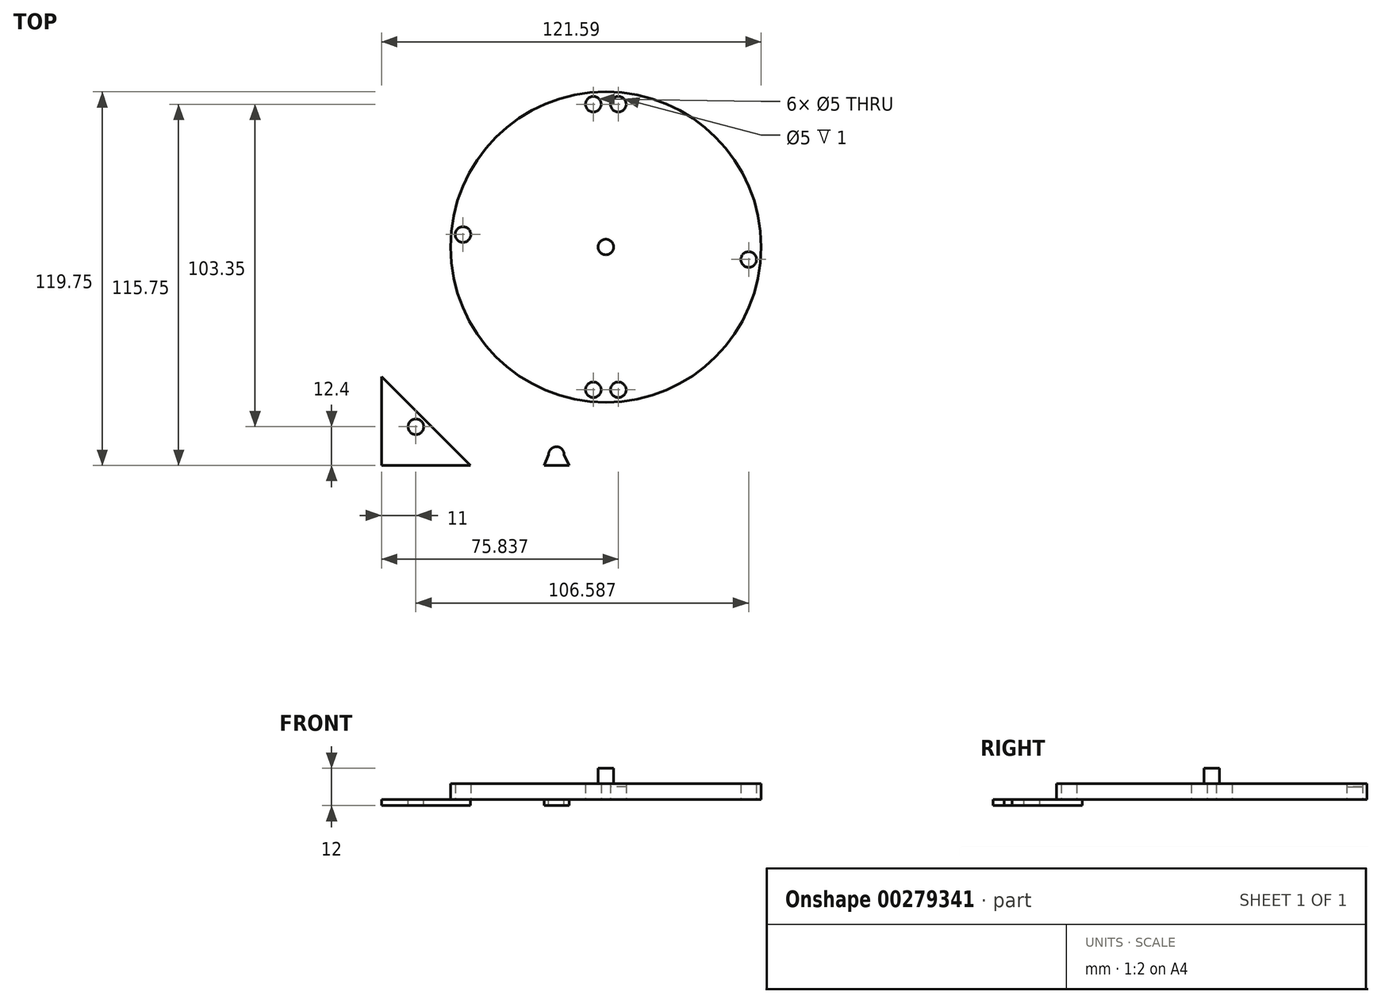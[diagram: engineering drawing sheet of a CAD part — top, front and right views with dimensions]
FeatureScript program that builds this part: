
annotation { "Feature Type Name" : "Feature", "Feature Type Description" : "" }
export const myFeature = defineFeature(function(context is Context, id is Id, definition is map)
    precondition{}
    {
        {
            var Q0;
            Q0=qCreatedBy(makeId("Top.planeOp"),FACE);
            var sketch = newSketch(context, id + "F0", { "sketchPlane" : qUnion([Q0])});
            skLineSegment(sketch, "E0.bottom", {"start": v(75, 70) * mm, "end": v(-75, 70) * mm});
            skLineSegment(sketch, "E0.top", {"start": v(75, -70) * mm, "end": v(-75, -70) * mm});
            skLineSegment(sketch, "E0.left", {"start": v(75, 70) * mm, "end": v(75, -70) * mm});
            skLineSegment(sketch, "E0.right", {"start": v(-75, 70) * mm, "end": v(-75, -70) * mm});
            skPoint(sketch, "E0.middle", {"position": v(0, 0) * mm});
            skSolve(sketch);
        }
        {
            var Q0;
            Q0=qSketchRegion(id+"F0",true);
            extrude(context, id + "F1", {"entities" : qUnion([Q0]), "depth" : 2 * mm});
        }
        {
            var Q0;
            Q0=makeQuery(id+"F1.opExtrude","CAP_FACE",FACE,{"disambiguationData":[OSD([sQuery(id+"F0.wireOp",EDGE,"E0.bottom"),sQuery(id+"F0.wireOp",EDGE,"E0.top"),sQuery(id+"F0.wireOp",EDGE,"E0.left"),sQuery(id+"F0.wireOp",EDGE,"E0.right")])],"isStart":false});
            var sketch = newSketch(context, id + "F2", { "sketchPlane" : qUnion([Q0])});
            skArc(sketch, "E1", {"start": v(-67.18, 6.35) * mm, "mid": v(-67.92, 8.12) * mm, "end": v(-69.68, 8.85) * mm});
            skArc(sketch, "E2.MirrorC", {"start": v(-67.18, -6.35) * mm, "mid": v(-67.92, -8.12) * mm, "end": v(-69.68, -8.85) * mm});
            skArc(sketch, "E3", {"start": v(-21.5, 66.52) * mm, "mid": v(-19, 64) * mm, "end": v(-16.5, 66.52) * mm});
            skCircle(sketch, "E4", {"center": v(-64, 57.6) * mm, "radius": 2.5 * mm});
            skArc(sketch, "E5.MirrorC", {"start": v(-21.5, -66.52) * mm, "mid": v(-19, -64) * mm, "end": v(-16.5, -66.52) * mm});
            skCircle(sketch, "E6.MirrorC", {"center": v(-64, -57.6) * mm, "radius": 2.5 * mm});
            skLineSegment(sketch, "E7", {"start": v(-21.5, 66.52) * mm, "end": v(-22.94, 70) * mm});
            skLineSegment(sketch, "E8.MirrorCS", {"start": v(-16.5, 66.52) * mm, "end": v(-14.88, 70) * mm});
            skLineSegment(sketch, "E9.MirrorCS", {"start": v(-16.5, -66.52) * mm, "end": v(-14.88, -70) * mm});
            skLineSegment(sketch, "E10.MirrorCS", {"start": v(-21.5, -66.52) * mm, "end": v(-22.94, -70) * mm});
            skLineSegment(sketch, "E11", {"start": v(-46.5, 70) * mm, "end": v(-75, 41.5) * mm});
            skLineSegment(sketch, "E12.MirrorCS", {"start": v(-46.5, -70) * mm, "end": v(-75, -41.5) * mm});
            skLineSegment(sketch, "E13", {"start": v(-69.68, 8.85) * mm, "end": v(-75, 8.85) * mm});
            skLineSegment(sketch, "E14", {"start": v(-67.18, -6.35) * mm, "end": v(-67.18, 6.35) * mm});
            skLineSegment(sketch, "E15.MirrorCS", {"start": v(-69.68, -8.85) * mm, "end": v(-75, -8.85) * mm});
            skSolve(sketch);
        }
        {
            var Q0;
            Q0=qSketchRegion(id+"F2",true);
            var Q1;
            Q1=makeQuery(id+"F2.imprint","IMPRINT",FACE,{"disambiguationData":[TD([[makeQuery(id+"F2.imprint","IMPRINT",EDGE,{"derivedFrom":sQuery(id+"F2.wireOp",EDGE,"E4")}),-1.0]])]});
            var Q2;
            Q2=makeQuery(id+"F2.imprint","IMPRINT",FACE,{"disambiguationData":[TD([[makeQuery(id+"F2.imprint","IMPRINT",EDGE,{"derivedFrom":sQuery(id+"F2.wireOp",EDGE,"E1")}),1.0]])]});
            var Q3;
            Q3=makeQuery(id+"F2.imprint","IMPRINT",FACE,{"disambiguationData":[TD([[makeQuery(id+"F2.imprint","IMPRINT",EDGE,{"derivedFrom":sQuery(id+"F2.wireOp",EDGE,"E5.MirrorC")}),-1.0]])]});
            var Q4;
            Q4=makeQuery(id+"F2.imprint","IMPRINT",FACE,{"disambiguationData":[TD([[makeQuery(id+"F2.imprint","IMPRINT",EDGE,{"derivedFrom":sQuery(id+"F2.wireOp",EDGE,"E3")}),1.0]])]});
            var Q5;
            Q5=makeQuery(id+"F2.imprint","IMPRINT",FACE,{"disambiguationData":[TD([[makeQuery(id+"F2.imprint","IMPRINT",EDGE,{"derivedFrom":sQuery(id+"F2.wireOp",EDGE,"E6.MirrorC")}),1.0]])]});
            extrude(context, id + "F3", {"entities" : qUnion([Q0, Q1, Q2, Q3, Q4, Q5]), "operationType" : NewBodyOperationType.REMOVE, "oppositeDirection" : true, "depth" : 5 * mm});
        }
        {
            var Q0;
            Q0=makeQuery(id+"F1.opExtrude","CAP_FACE",FACE,{"disambiguationData":[OSD([sQuery(id+"F0.wireOp",EDGE,"E0.bottom"),sQuery(id+"F0.wireOp",EDGE,"E0.top"),sQuery(id+"F0.wireOp",EDGE,"E0.left"),sQuery(id+"F0.wireOp",EDGE,"E0.right")])],"isStart":false});
            var sketch = newSketch(context, id + "F4", { "sketchPlane" : qUnion([Q0])});
            skCircle(sketch, "E16", {"center": v(-3.16, 0) * mm, "radius": 49.75 * mm});
            skLineSegment(sketch, "E17", {"start": v(-3.16, 0) * mm, "end": v(-53.16, 0) * mm});
            skLineSegment(sketch, "E18", {"start": v(-3.16, 0) * mm, "end": v(-3.16, 49.75) * mm});
            skLineSegment(sketch, "E19", {"start": v(-3.16, 0) * mm, "end": v(46.59, 0) * mm});
            skLineSegment(sketch, "E20", {"start": v(-3.16, 0) * mm, "end": v(-3.16, -49.75) * mm});
            skCircle(sketch, "E21", {"center": v(-7.16, 45.75) * mm, "radius": 2.5 * mm});
            skCircle(sketch, "E22.MirrorC", {"center": v(0.84, 45.75) * mm, "radius": 2.5 * mm});
            skCircle(sketch, "E23.1.0", {"center": v(-48.91, 4) * mm, "radius": 2.5 * mm});
            skCircle(sketch, "E23.1.1", {"center": v(-48.91, -4) * mm, "radius": 2.5 * mm});
            skCircle(sketch, "E23.2.0", {"center": v(-7.16, -45.75) * mm, "radius": 2.5 * mm});
            skCircle(sketch, "E23.2.1", {"center": v(0.84, -45.75) * mm, "radius": 2.5 * mm});
            skCircle(sketch, "E23.3.0", {"center": v(42.59, -4) * mm, "radius": 2.5 * mm});
            skCircle(sketch, "E23.3.1", {"center": v(42.59, 4) * mm, "radius": 2.5 * mm});
            skCircle(sketch, "E24", {"center": v(-3.16, 0) * mm, "radius": 2.5 * mm});
            skSolve(sketch);
        }
        {
            var Q0;
            Q0=makeQuery(id+"F4.imprint","IMPRINT",FACE,{"disambiguationData":[TD([[makeQuery(id+"F4.imprint","IMPRINT",EDGE,{"derivedFrom":sQuery(id+"F4.wireOp",EDGE,"E21")}),-1.0]])]});
            var Q1;
            Q1=makeQuery(id+"F4.imprint","IMPRINT",FACE,{"disambiguationData":[TD([[makeQuery(id+"F4.imprint","IMPRINT",EDGE,{"derivedFrom":sQuery(id+"F4.wireOp",EDGE,"E23.2.1")}),-1.0]])]});
            var Q2;
            Q2=makeQuery(id+"F4.imprint","IMPRINT",FACE,{"disambiguationData":[TD([[makeQuery(id+"F4.imprint","IMPRINT",EDGE,{"derivedFrom":sQuery(id+"F4.wireOp",EDGE,"E22.MirrorC")}),-1.0]])]});
            var Q3;
            Q3=makeQuery(id+"F4.imprint","IMPRINT",FACE,{"disambiguationData":[TD([[makeQuery(id+"F4.imprint","IMPRINT",EDGE,{"derivedFrom":sQuery(id+"F4.wireOp",EDGE,"E23.3.1")}),1.0]])]});
            var Q4;
            Q4=makeQuery(id+"F4.imprint","IMPRINT",FACE,{"disambiguationData":[TD([[makeQuery(id+"F4.imprint","IMPRINT",EDGE,{"derivedFrom":sQuery(id+"F4.wireOp",EDGE,"E23.2.0")}),-1.0]])]});
            var Q5;
            Q5=makeQuery(id+"F4.imprint","IMPRINT",FACE,{"disambiguationData":[TD([[makeQuery(id+"F4.imprint","IMPRINT",EDGE,{"derivedFrom":sQuery(id+"F4.wireOp",EDGE,"E23.1.1")}),1.0]])]});
            var Q6;
            {var subQ1=sQuery(id+"F4.wireOp",EDGE,"E17");var subQ3=sQuery(id+"F4.wireOp",EDGE,"E24");var subQ4=makeQuery(id+"F4.imprint","INTERSECT",VERTEX,{"derivedFrom":[subQ1,subQ3]});Q6=makeQuery(id+"F4.imprint","IMPRINT",FACE,{"disambiguationData":[TD([[makeQuery(id+"F4.imprint","IMPRINT",EDGE,{"disambiguationData":[TD([[subQ4,-1.0]])],"derivedFrom":subQ3}),1.0]])]});}
            var Q7;
            {var subQ1=sQuery(id+"F4.wireOp",EDGE,"E18");var subQ3=sQuery(id+"F4.wireOp",EDGE,"E24");var subQ4=makeQuery(id+"F4.imprint","INTERSECT",VERTEX,{"derivedFrom":[subQ1,subQ3]});Q7=makeQuery(id+"F4.imprint","IMPRINT",FACE,{"disambiguationData":[TD([[makeQuery(id+"F4.imprint","IMPRINT",EDGE,{"disambiguationData":[TD([[subQ4,1.0]])],"derivedFrom":subQ3}),1.0]])]});}
            var Q8;
            {var subQ1=sQuery(id+"F4.wireOp",EDGE,"E19");var subQ3=sQuery(id+"F4.wireOp",EDGE,"E24");var subQ4=makeQuery(id+"F4.imprint","INTERSECT",VERTEX,{"derivedFrom":[subQ1,subQ3]});Q8=makeQuery(id+"F4.imprint","IMPRINT",FACE,{"disambiguationData":[TD([[makeQuery(id+"F4.imprint","IMPRINT",EDGE,{"disambiguationData":[TD([[subQ4,1.0]])],"derivedFrom":subQ3}),1.0]])]});}
            var Q9;
            {var subQ1=sQuery(id+"F4.wireOp",EDGE,"E17");var subQ3=sQuery(id+"F4.wireOp",EDGE,"E24");var subQ4=makeQuery(id+"F4.imprint","INTERSECT",VERTEX,{"derivedFrom":[subQ1,subQ3]});Q9=makeQuery(id+"F4.imprint","IMPRINT",FACE,{"disambiguationData":[TD([[makeQuery(id+"F4.imprint","IMPRINT",EDGE,{"disambiguationData":[TD([[subQ4,1.0]])],"derivedFrom":subQ3}),1.0]])]});}
            extrude(context, id + "F5", {"entities" : qUnion([Q0, Q1, Q2, Q3, Q4, Q5, Q6, Q7, Q8, Q9]), "operationType" : NewBodyOperationType.ADD, "depth" : 5 * mm});
        }
        {
            var Q0;
            Q0=makeQuery(id+"F4.imprint","IMPRINT",FACE,{"disambiguationData":[TD([[makeQuery(id+"F4.imprint","IMPRINT",EDGE,{"derivedFrom":sQuery(id+"F4.wireOp",EDGE,"E23.1.1")}),-1.0]])]});
            var Q1;
            Q1=makeQuery(id+"F4.imprint","IMPRINT",FACE,{"disambiguationData":[TD([[makeQuery(id+"F4.imprint","IMPRINT",EDGE,{"derivedFrom":sQuery(id+"F4.wireOp",EDGE,"E22.MirrorC")}),1.0]])]});
            extrude(context, id + "F6", {"entities" : qUnion([Q0, Q1]), "operationType" : NewBodyOperationType.ADD, "depth" : 4 * mm});
        }
        {
            var Q0;
            {var subQ1=sQuery(id+"F4.wireOp",EDGE,"E19");var subQ3=sQuery(id+"F4.wireOp",EDGE,"E24");var subQ4=makeQuery(id+"F4.imprint","INTERSECT",VERTEX,{"derivedFrom":[subQ1,subQ3]});Q0=makeQuery(id+"F4.imprint","IMPRINT",FACE,{"disambiguationData":[TD([[makeQuery(id+"F4.imprint","IMPRINT",EDGE,{"disambiguationData":[TD([[subQ4,1.0]])],"derivedFrom":subQ3}),1.0]])]});}
            var Q1;
            {var subQ1=sQuery(id+"F4.wireOp",EDGE,"E18");var subQ3=sQuery(id+"F4.wireOp",EDGE,"E24");var subQ4=makeQuery(id+"F4.imprint","INTERSECT",VERTEX,{"derivedFrom":[subQ1,subQ3]});Q1=makeQuery(id+"F4.imprint","IMPRINT",FACE,{"disambiguationData":[TD([[makeQuery(id+"F4.imprint","IMPRINT",EDGE,{"disambiguationData":[TD([[subQ4,1.0]])],"derivedFrom":subQ3}),1.0]])]});}
            var Q2;
            {var subQ1=sQuery(id+"F4.wireOp",EDGE,"E17");var subQ3=sQuery(id+"F4.wireOp",EDGE,"E24");var subQ4=makeQuery(id+"F4.imprint","INTERSECT",VERTEX,{"derivedFrom":[subQ1,subQ3]});Q2=makeQuery(id+"F4.imprint","IMPRINT",FACE,{"disambiguationData":[TD([[makeQuery(id+"F4.imprint","IMPRINT",EDGE,{"disambiguationData":[TD([[subQ4,1.0]])],"derivedFrom":subQ3}),1.0]])]});}
            var Q3;
            {var subQ1=sQuery(id+"F4.wireOp",EDGE,"E17");var subQ3=sQuery(id+"F4.wireOp",EDGE,"E24");var subQ4=makeQuery(id+"F4.imprint","INTERSECT",VERTEX,{"derivedFrom":[subQ1,subQ3]});Q3=makeQuery(id+"F4.imprint","IMPRINT",FACE,{"disambiguationData":[TD([[makeQuery(id+"F4.imprint","IMPRINT",EDGE,{"disambiguationData":[TD([[subQ4,-1.0]])],"derivedFrom":subQ3}),1.0]])]});}
            extrude(context, id + "F7", {"entities" : qUnion([Q0, Q1, Q2, Q3]), "operationType" : NewBodyOperationType.ADD, "depth" : 10 * mm});
        }
    });
